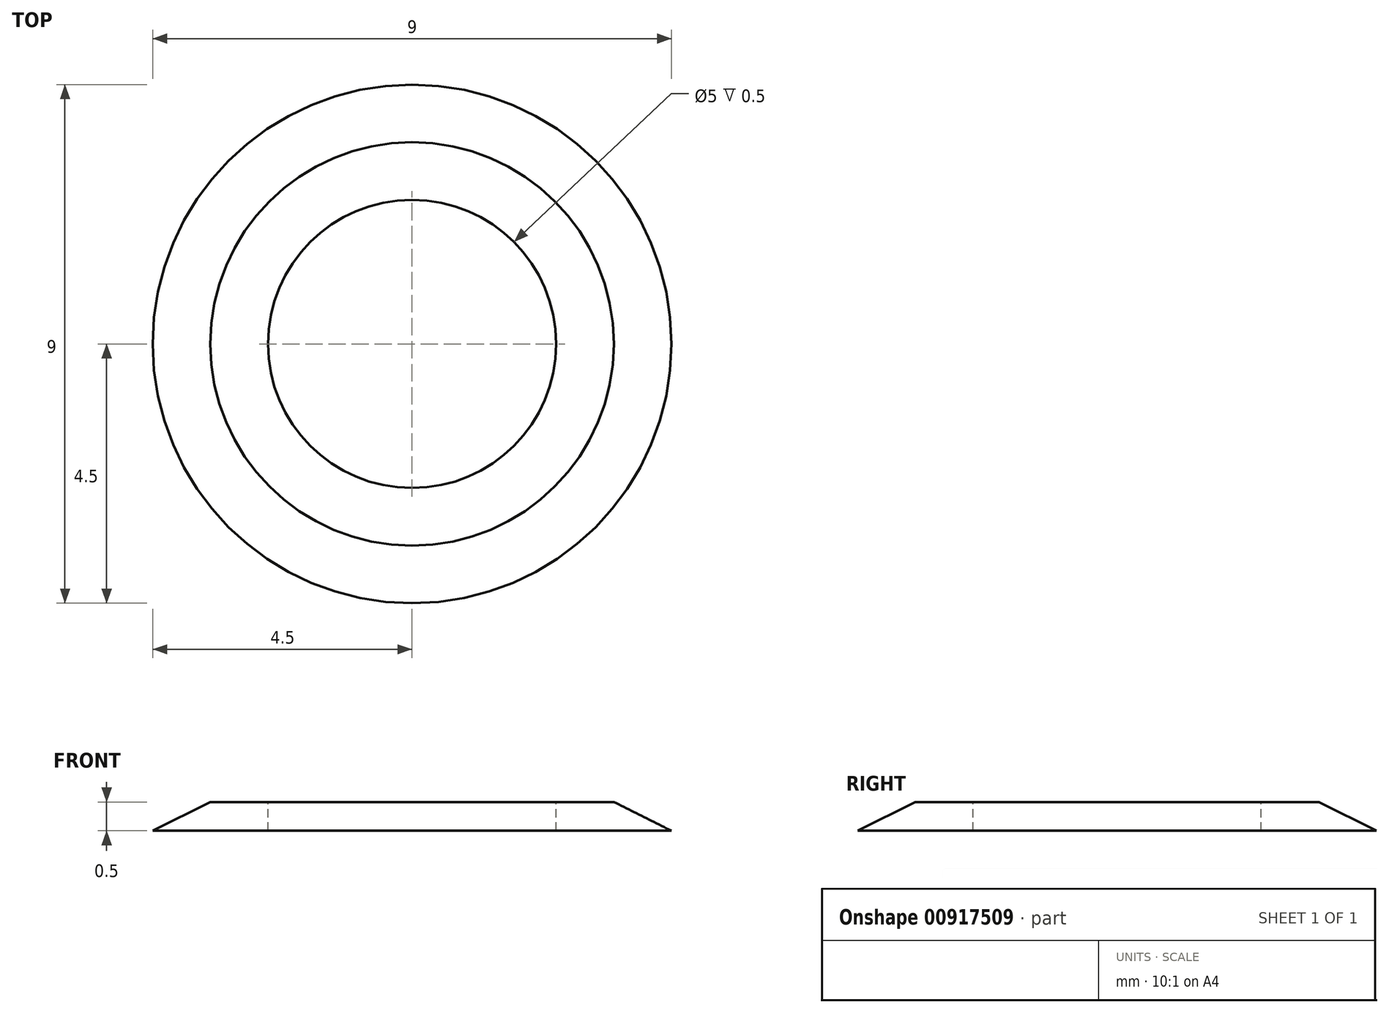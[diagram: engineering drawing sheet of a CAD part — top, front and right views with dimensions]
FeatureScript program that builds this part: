
annotation { "Feature Type Name" : "Feature", "Feature Type Description" : "" }
export const myFeature = defineFeature(function(context is Context, id is Id, definition is map)
    precondition{}
    {
        {
            var Q0;
            Q0=qCreatedBy(makeId("Front.planeOp"),FACE);
            var sketch = newSketch(context, id + "F0", { "sketchPlane" : qUnion([Q0])});
            skLineSegment(sketch, "E0", {"start": v(4.5, 0) * mm, "end": v(3.5, 0.5) * mm});
            skLineSegment(sketch, "E1", {"start": v(3.5, 0.5) * mm, "end": v(2.5, 0.5) * mm});
            skLineSegment(sketch, "E2", {"start": v(0, 3.85) * mm, "end": v(0, 0) * mm, "construction": true});
            skLineSegment(sketch, "E3", {"start": v(2.5, 0) * mm, "end": v(2.5, 0.5) * mm});
            skLineSegment(sketch, "E4", {"start": v(2.5, 0) * mm, "end": v(4.5, 0) * mm});
            skSolve(sketch);
        }
        {
            var Q0;
            Q0=makeQuery(id+"F0.imprint","IMPRINT",FACE,{"disambiguationData":[TD([[makeQuery(id+"F0.imprint","IMPRINT",EDGE,{"derivedFrom":sQuery(id+"F0.wireOp",EDGE,"E0")}),1.0]])]});
            var Q1;
            Q1=sQuery(id+"F0.wireOp",EDGE,"E2");
            revolve(context, id + "F1", {"surfaceOperationType" : NewSurfaceOperationType.NEW, "entities" : qUnion([Q0]), "axis" : qUnion([Q1]), "revolveType" : RevolveType.FULL});
        }
    });
